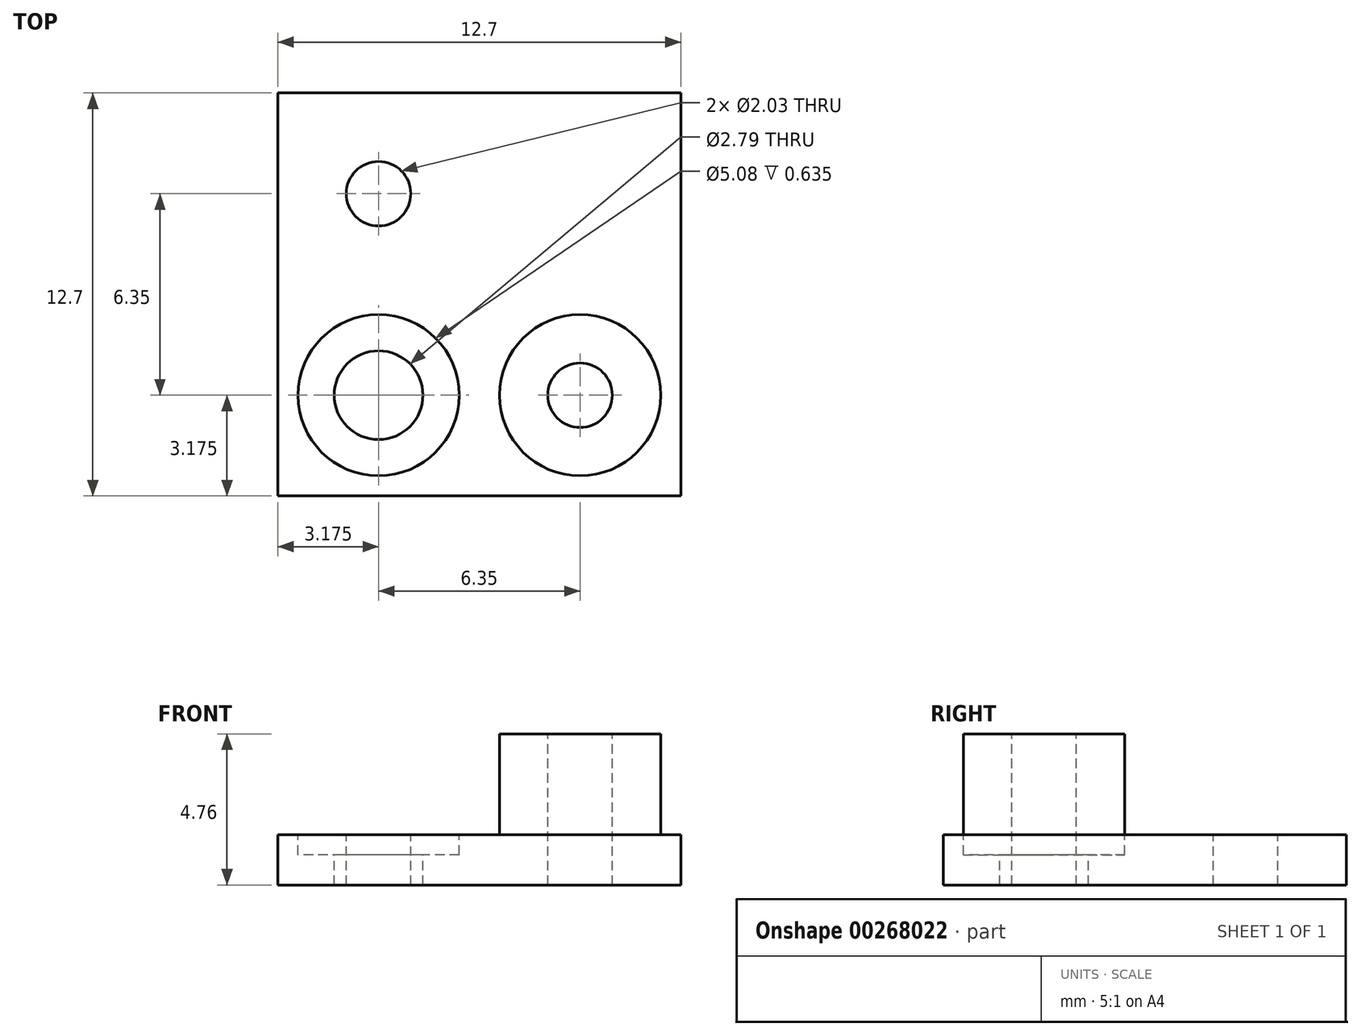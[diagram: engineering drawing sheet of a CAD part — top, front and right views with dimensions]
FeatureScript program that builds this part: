
annotation { "Feature Type Name" : "Feature", "Feature Type Description" : "" }
export const myFeature = defineFeature(function(context is Context, id is Id, definition is map)
    precondition{}
    {
        {
            var Q0;
            Q0=qCreatedBy(makeId("Top.planeOp"),FACE);
            var sketch = newSketch(context, id + "F0", { "sketchPlane" : qUnion([Q0])});
            skLineSegment(sketch, "E0.bottom", {"start": v(6.35, -6.35) * mm, "end": v(-6.35, -6.35) * mm});
            skLineSegment(sketch, "E0.top", {"start": v(6.35, 6.35) * mm, "end": v(-6.35, 6.35) * mm});
            skLineSegment(sketch, "E0.left", {"start": v(6.35, -6.35) * mm, "end": v(6.35, 6.35) * mm});
            skLineSegment(sketch, "E0.right", {"start": v(-6.35, -6.35) * mm, "end": v(-6.35, 6.35) * mm});
            skPoint(sketch, "E0.middle", {"position": v(0, 0) * mm});
            skSolve(sketch);
        }
        {
            var Q0;
            Q0=makeQuery(id+"F0.imprint","IMPRINT",FACE,{"disambiguationData":[TD([[makeQuery(id+"F0.imprint","IMPRINT",EDGE,{"derivedFrom":sQuery(id+"F0.wireOp",EDGE,"E0.bottom")}),-1.0]])]});
            extrude(context, id + "F1", {"entities" : qUnion([Q0]), "depth" : 1.59 * mm, "offsetDistance" : 25.4 * mm});
        }
        {
            var Q0;
            Q0=makeQuery(id+"F1.opExtrude","CAP_FACE",FACE,{"disambiguationData":[OSD([sQuery(id+"F0.wireOp",EDGE,"E0.bottom"),sQuery(id+"F0.wireOp",EDGE,"E0.top"),sQuery(id+"F0.wireOp",EDGE,"E0.left"),sQuery(id+"F0.wireOp",EDGE,"E0.right")])],"isStart":false});
            var sketch = newSketch(context, id + "F2", { "sketchPlane" : qUnion([Q0])});
            skLineSegment(sketch, "E1.bottom", {"start": v(0, 0) * mm, "end": v(-6.35, 0) * mm, "construction": true});
            skLineSegment(sketch, "E1.top", {"start": v(0, -6.35) * mm, "end": v(-6.35, -6.35) * mm, "construction": true});
            skLineSegment(sketch, "E1.left", {"start": v(0, 0) * mm, "end": v(0, -6.35) * mm, "construction": true});
            skLineSegment(sketch, "E1.right", {"start": v(-6.35, 0) * mm, "end": v(-6.35, -6.35) * mm, "construction": true});
            skLineSegment(sketch, "E2.bottom", {"start": v(0, 0) * mm, "end": v(6.35, 0) * mm, "construction": true});
            skLineSegment(sketch, "E2.top", {"start": v(0, 6.35) * mm, "end": v(6.35, 6.35) * mm, "construction": true});
            skLineSegment(sketch, "E2.left", {"start": v(0, 0) * mm, "end": v(0, 6.35) * mm, "construction": true});
            skLineSegment(sketch, "E2.right", {"start": v(6.35, 0) * mm, "end": v(6.35, 6.35) * mm, "construction": true});
            skLineSegment(sketch, "E3", {"start": v(0, 0) * mm, "end": v(6.35, 6.35) * mm, "construction": true});
            skLineSegment(sketch, "E4", {"start": v(6.35, -6.35) * mm, "end": v(0, 0) * mm, "construction": true});
            skLineSegment(sketch, "E5", {"start": v(0, 0) * mm, "end": v(-6.35, -6.35) * mm, "construction": true});
            skLineSegment(sketch, "E6", {"start": v(-6.35, 6.35) * mm, "end": v(0, 0) * mm, "construction": true});
            skCircle(sketch, "E7", {"center": v(3.18, -3.18) * mm, "radius": 1.02 * mm});
            skCircle(sketch, "E8", {"center": v(3.18, -3.18) * mm, "radius": 2.54 * mm});
            skCircle(sketch, "E9", {"center": v(-3.18, 3.18) * mm, "radius": 1.02 * mm});
            skCircle(sketch, "E10", {"center": v(-3.17, -3.18) * mm, "radius": 2.54 * mm});
            skCircle(sketch, "E11", {"center": v(-3.17, -3.18) * mm, "radius": 1.4 * mm});
            skSolve(sketch);
        }
        {
            var Q0;
            Q0=makeQuery(id+"F2.imprint","IMPRINT",FACE,{"disambiguationData":[TD([[makeQuery(id+"F2.imprint","IMPRINT",EDGE,{"derivedFrom":sQuery(id+"F2.wireOp",EDGE,"E9")}),1.0]])]});
            var Q1;
            Q1=makeQuery(id+"F2.imprint","IMPRINT",FACE,{"disambiguationData":[TD([[makeQuery(id+"F2.imprint","IMPRINT",EDGE,{"derivedFrom":sQuery(id+"F2.wireOp",EDGE,"E7")}),1.0]])]});
            var Q2;
            Q2=makeQuery(id+"F2.imprint","IMPRINT",FACE,{"disambiguationData":[TD([[makeQuery(id+"F2.imprint","IMPRINT",EDGE,{"derivedFrom":sQuery(id+"F2.wireOp",EDGE,"E11")}),1.0]])]});
            extrude(context, id + "F3", {"entities" : qUnion([Q0, Q1, Q2]), "operationType" : NewBodyOperationType.REMOVE, "oppositeDirection" : true, "depth" : 6.35 * mm});
        }
        {
            var Q0;
            Q0=makeQuery(id+"F2.imprint","IMPRINT",FACE,{"disambiguationData":[TD([[makeQuery(id+"F2.imprint","IMPRINT",EDGE,{"derivedFrom":sQuery(id+"F2.wireOp",EDGE,"E7")}),-1.0]])]});
            extrude(context, id + "F4", {"entities" : qUnion([Q0]), "operationType" : NewBodyOperationType.ADD, "depth" : 3.17 * mm});
        }
        {
            var Q0;
            Q0=makeQuery(id+"F2.imprint","IMPRINT",FACE,{"disambiguationData":[TD([[makeQuery(id+"F2.imprint","IMPRINT",EDGE,{"derivedFrom":sQuery(id+"F2.wireOp",EDGE,"E10")}),1.0]])]});
            extrude(context, id + "F5", {"entities" : qUnion([Q0]), "operationType" : NewBodyOperationType.REMOVE, "oppositeDirection" : true, "depth" : 0.64 * mm, "offsetDistance" : 25.4 * mm});
        }
    });
